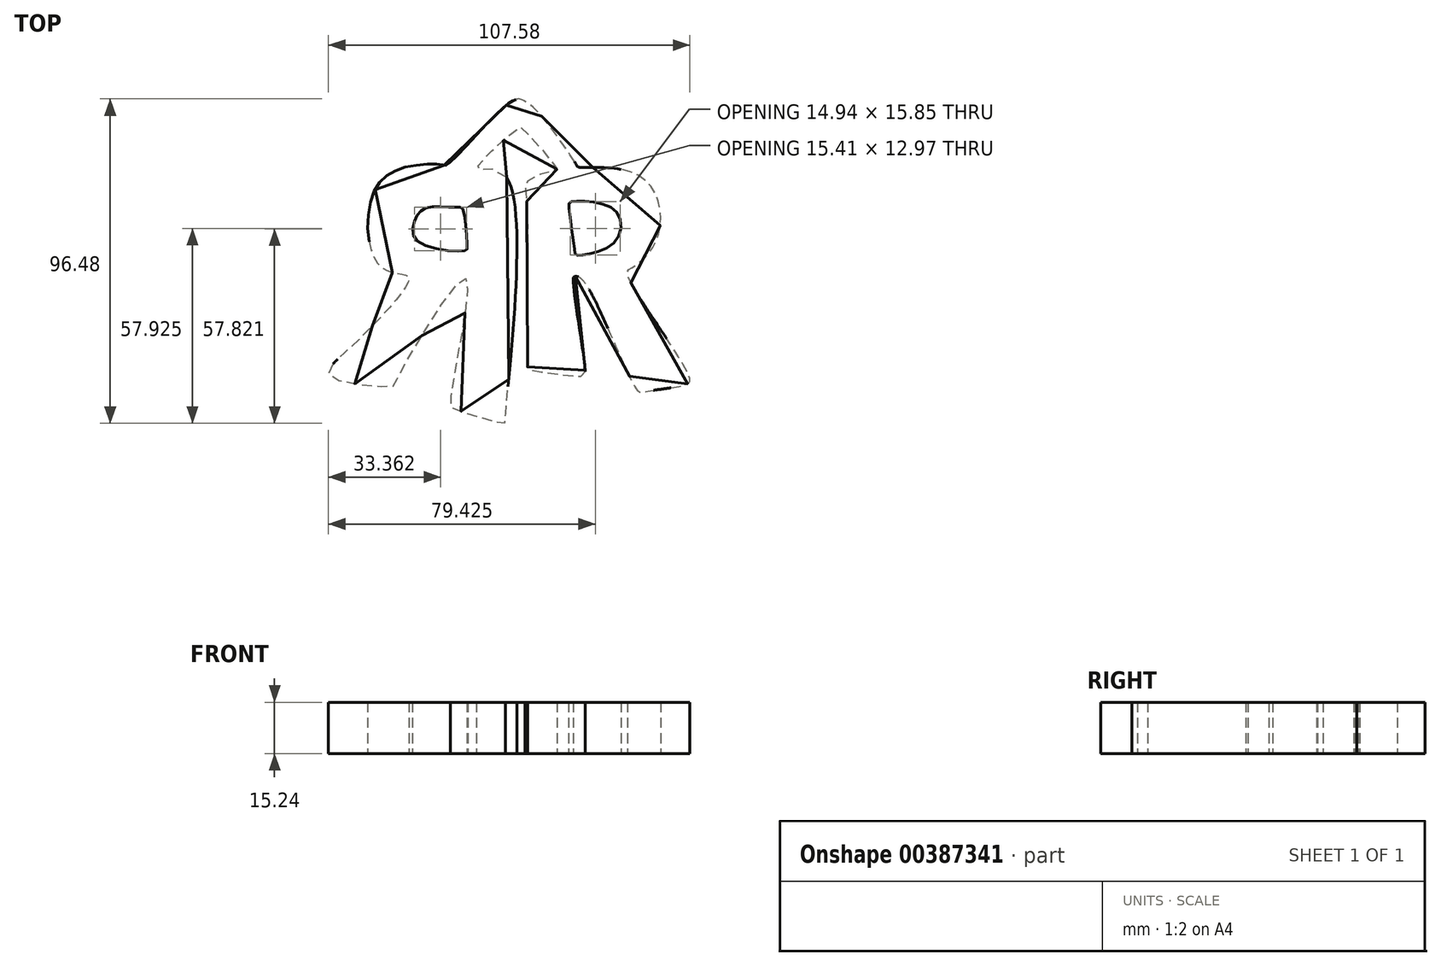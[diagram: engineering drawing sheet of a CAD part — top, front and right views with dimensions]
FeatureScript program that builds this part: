
annotation { "Feature Type Name" : "Feature", "Feature Type Description" : "" }
export const myFeature = defineFeature(function(context is Context, id is Id, definition is map)
    precondition{}
    {
        {
            var Q0;
            Q0=qCreatedBy(makeId("Top.planeOp"),FACE);
            var sketch = newSketch(context, id + "F0", { "sketchPlane" : qUnion([Q0])});
            skFitSpline(sketch, "E0", {"points": [v(-3.53, 36.9) * mm, v(-11.77, 39.08) * mm, v(-12.44, 39.75) * mm, v(0, 51.69) * mm, v(1.18, 51.52) * mm, v(11.43, 39.25) * mm, v(9.58, 38.74) * mm, v(2.19, 35.38) * mm, v(2.19, 33.37) * mm, v(2.69, -19.25) * mm, v(3.53, -20.42) * mm, v(18.66, -22.27) * mm, v(19.83, -21.1) * mm, v(16.3, 5.46) * mm, v(16.8, 7.48) * mm, v(19.67, 5.63) * mm, v(35.13, -26.14) * mm, v(37.65, -26.81) * mm, v(49.59, -24.8) * mm, v(50.76, -22.27) * mm, v(32.44, 7.98) * mm, v(33.95, 10.17) * mm, v(41.52, 19.41) * mm, v(36.14, 37.23) * mm, v(18.15, 39.92) * mm, v(17.15, 40.76) * mm, v(6.22, 55.89) * mm, v(1.18, 59.92) * mm, v(0, 60.26) * mm, v(-1.51, 59.76) * mm, v(-6.22, 56.06) * mm, v(-21.35, 40.6) * mm, v(-22.36, 40.6) * mm, v(-34.3, 39.75) * mm, v(-43.87, 30.34) * mm, v(-41.35, 10.67) * mm, v(-33.62, 7.82) * mm, v(-32.6, 6.3) * mm, v(-50.43, -14.04) * mm, v(-55.97, -22.27) * mm, v(-37.99, -25.3) * mm, v(-36.48, -23.78) * mm, v(-16.64, 6.64) * mm, v(-15.13, 4.62) * mm, v(-20.34, -30) * mm, v(-18.66, -32.19) * mm, v(-4.37, -36.22) * mm, v(-3.87, -34.71) * mm, v(-3.53, 36.9) * mm]});
            skFitSpline(sketch, "E1", {"points": [v(-16.64, 27.48) * mm, v(-18.15, 27.99) * mm, v(-26.9, 27.99) * mm, v(-30.6, 24.8) * mm, v(-30.26, 18.07) * mm, v(-15.97, 15.04) * mm, v(-15.3, 16.22) * mm, v(-16.64, 27.48) * mm]});
            skFitSpline(sketch, "E2", {"points": [v(16.64, 15.55) * mm, v(14.96, 28.15) * mm, v(15.3, 29.5) * mm, v(21.01, 29.67) * mm, v(29.42, 26.3) * mm, v(29.25, 18.4) * mm, v(21.18, 14.2) * mm, v(17.15, 13.87) * mm, v(16.64, 15.55) * mm]});
            skSolve(sketch);
        }
        {
            var Q0;
            Q0=makeQuery(id+"F0.imprint","IMPRINT",FACE,{"disambiguationData":[TD([[makeQuery(id+"F0.imprint","IMPRINT",EDGE,{"derivedFrom":sQuery(id+"F0.wireOp",EDGE,"E0")}),1.0]])]});
            extrude(context, id + "F1", {"entities" : qUnion([Q0]), "depth" : 15.24 * mm});
        }
    });
